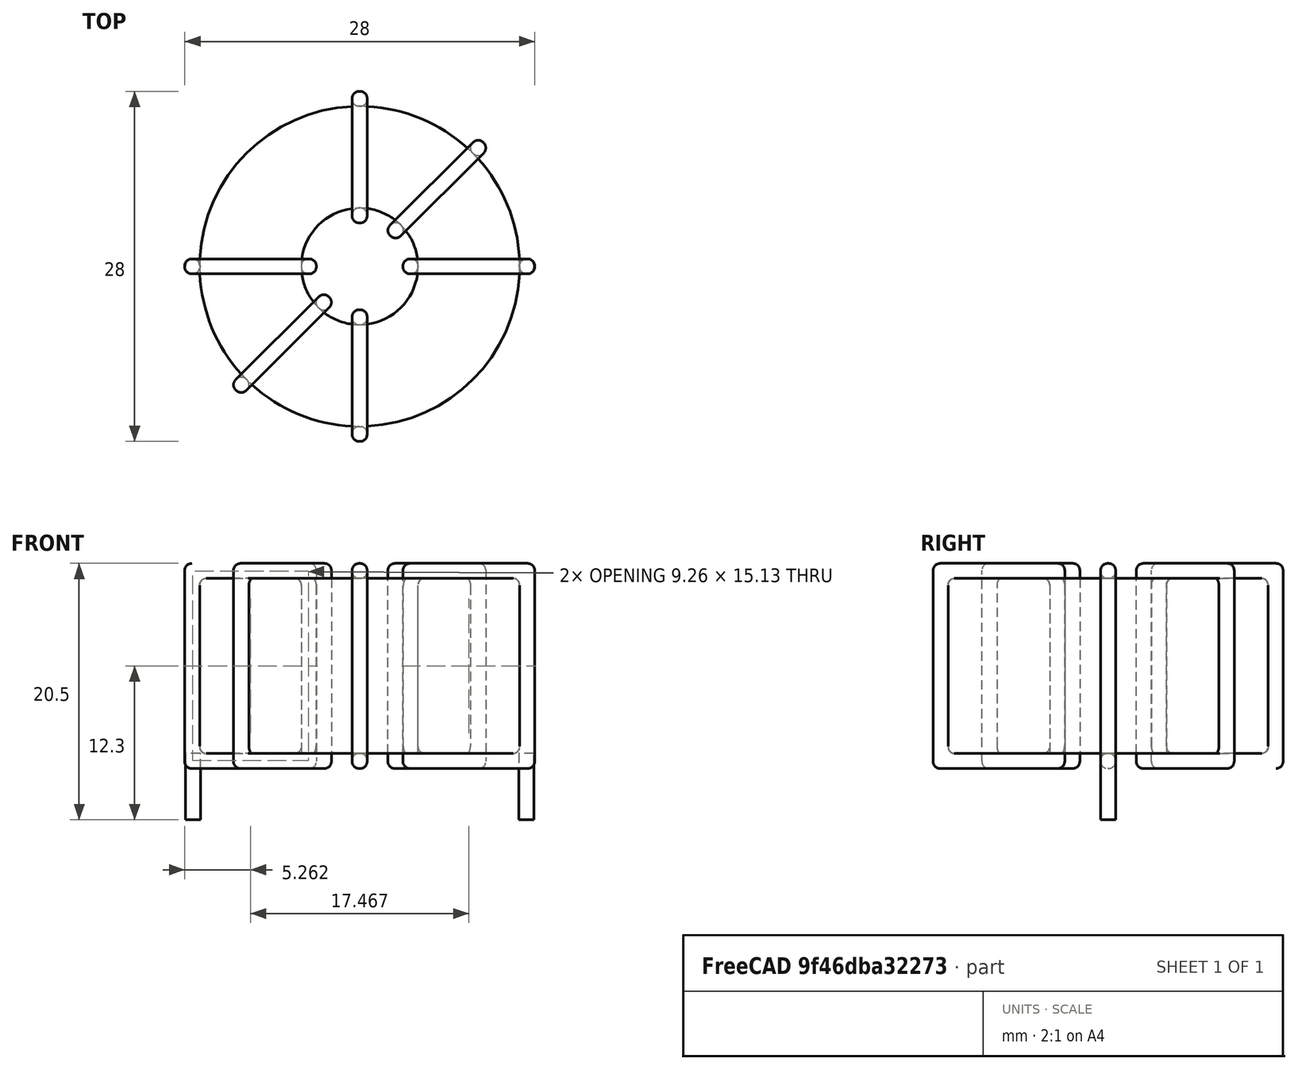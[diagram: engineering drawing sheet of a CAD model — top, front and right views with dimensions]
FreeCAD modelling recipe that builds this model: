
FCSTD DOCUMENT  (FreeCAD 0.16R6703 (Git))
Label: L_Toroid_Horizontal_D28.0mm_P26.67mm_Bourns_2200series
License: All rights reserved
LicenseURL: http://en.wikipedia.org/wiki/All_rights_reserved
objects: Sketcher::SketchObject×6, PartDesign::Pad×6, PartDesign::Fillet×5, Spreadsheet::Sheet×1
note: 23 computed .brp shape members not serialized (recipe doc carries the construction recipe); baked Part::Feature solids carry a one-line shape summary decoded from their .brp

FEATURE [Spreadsheet::Sheet] Spreadsheet  label="dimensions"
  cells = A1=Wx; B1(Wx)=28; C1(WW)=9.333333333333334; D1=28; A2=Wy; B2(Wy)=28; D2=28; A3=RM; B3(RMx)=26.67; C3(RMy)=0; A4=d_wire; B4(d_wire)=1.2; A5=H; B5(H)=14; A6=offsetx; B6(offsetx)=0.6649999999999992
FEATURE [Sketcher::SketchObject] Sketch
  Placement = pos=(0,0,1.7) rot=(0,0,1;0rad)
  expr: Placement.Base.z = 0.5 + Spreadsheet.d_wire
  expr: Constraints[0] = Spreadsheet.Wx / 2 - Spreadsheet.d_wire
  expr: Constraints[4] = Spreadsheet.WW / 2
  expr: Constraints[2] = Spreadsheet.RMy / 2
  expr: Constraints[1] = Spreadsheet.RMx / 2
  sketch-geometry (2):
    g0: Circle CenterX=13.335 CenterY=0 CenterZ=0 NormalX=0 NormalY=0 NormalZ=1 Radius=12.8
    g1: Circle CenterX=13.335 CenterY=0 CenterZ=0 NormalX=0 NormalY=0 NormalZ=1 Radius=4.66667
  constraints (5):
    c: Radius(g0) = 12.8
    c: DistanceX(g-1,g0) = 13.335
    c: DistanceY(g-1,g0) = 0
    c: Coincident(g1,g0)
    c: Radius(g1) = 4.66667
FEATURE [PartDesign::Pad] Pad
  Length = 14
  Length2 = 100
  Placement = pos=(0,0,1.7) rot=(0,0,1;0rad)
  Sketch = -> Sketch
  Type = 0
  expr: Length = Spreadsheet.H
FEATURE [Sketcher::SketchObject] Sketch001
  Placement = pos=(0,0,1.1) rot=(0,0,1;0rad)
  expr: Placement.Base.z = 0.5 + Spreadsheet.d_wire * 0.5
  expr: Constraints[4] = Spreadsheet.RMx
  expr: Constraints[2] = Spreadsheet.RMy
  expr: Constraints[1] = Spreadsheet.d_wire / 2
  sketch-geometry (2):
    g0: Circle CenterX=0 CenterY=0 CenterZ=0 NormalX=0 NormalY=0 NormalZ=1 Radius=0.6
    g1: Circle CenterX=26.67 CenterY=0 CenterZ=0 NormalX=0 NormalY=0 NormalZ=1 Radius=0.6
  constraints (5):
    c: Equal(g0,g1)
    c: Radius(g0) = 0.6
    c: DistanceY(g-1,g1) = 0
    c: Coincident(g0,g-1)
    c: DistanceX(g-1,g1) = 26.67
FEATURE [PartDesign::Pad] Pad001
  Length = 0.6
  Length2 = 4.7
  Placement = pos=(0,0,1.1) rot=(0,0,1;0rad)
  Reversed = true
  Sketch = -> Sketch001
  Type = 4
  expr: Length2 = 3.5 + Spreadsheet.d_wire
  expr: Length = Spreadsheet.d_wire / 2
FEATURE [PartDesign::Fillet] Fillet
  Base = -> Pad [Edge6,Edge3,Edge2]
  Placement = pos=(0,0,1.7) rot=(0,0,1;0rad)
  Radius = 0.5
FEATURE [Sketcher::SketchObject] Sketch003
  Placement = pos=(13.335,0,0) rot=(1,0,0;1.5708rad)
  expr: Placement.Base.x = Spreadsheet.RMx / 2
  expr: Constraints[49] = Spreadsheet.Wx - Spreadsheet.d_wire * 2
  expr: Constraints[44] = Spreadsheet.d_wire
  expr: Constraints[23] = Spreadsheet.H
  expr: Constraints[22] = Spreadsheet.Wx / 2 - Spreadsheet.d_wire
  expr: Placement.Base.y = Spreadsheet.RMy / 2
  expr: Constraints[21] = (Spreadsheet.Wx - Spreadsheet.WW) / 2 - Spreadsheet.d_wire
  expr: Constraints[19] = Spreadsheet.d_wire
  expr: Constraints[17] = Spreadsheet.d_wire
  expr: Constraints[18] = Spreadsheet.d_wire
  expr: Constraints[16] = Spreadsheet.d_wire
  sketch-geometry (16):
    g0: LineSegment StartX=-3.46667 StartY=0.5 StartZ=0 EndX=-14 EndY=0.5 EndZ=0
    g1: LineSegment StartX=-14 StartY=0.5 StartZ=0 EndX=-14 EndY=16.9 EndZ=0
    g2: LineSegment StartX=-14 StartY=16.9 StartZ=0 EndX=-3.46667 EndY=16.9 EndZ=0
    g3: LineSegment StartX=-3.46667 StartY=16.9 StartZ=0 EndX=-3.46667 EndY=0.5 EndZ=0
    g4: LineSegment StartX=-12.8 StartY=15.7 StartZ=0 EndX=-4.66667 EndY=15.7 EndZ=0
    g5: LineSegment StartX=-4.66667 StartY=15.7 StartZ=0 EndX=-4.66667 EndY=1.7 EndZ=0
    g6: LineSegment StartX=-4.66667 StartY=1.7 StartZ=0 EndX=-12.8 EndY=1.7 EndZ=0
    g7: LineSegment StartX=-12.8 StartY=1.7 StartZ=0 EndX=-12.8 EndY=15.7 EndZ=0
    g8: LineSegment StartX=3.46667 StartY=16.9 StartZ=0 EndX=14 EndY=16.9 EndZ=0
    g9: LineSegment StartX=14 StartY=16.9 StartZ=0 EndX=14 EndY=0.5 EndZ=0
    g10: LineSegment StartX=14 StartY=0.5 StartZ=0 EndX=3.46667 EndY=0.5 EndZ=0
    g11: LineSegment StartX=3.46667 StartY=0.5 StartZ=0 EndX=3.46667 EndY=16.9 EndZ=0
    g12: LineSegment StartX=4.66667 StartY=15.7 StartZ=0 EndX=12.8 EndY=15.7 EndZ=0
    g13: LineSegment StartX=12.8 StartY=15.7 StartZ=0 EndX=12.8 EndY=1.7 EndZ=0
    g14: LineSegment StartX=12.8 StartY=1.7 StartZ=0 EndX=4.66667 EndY=1.7 EndZ=0
    g15: LineSegment StartX=4.66667 StartY=1.7 StartZ=0 EndX=4.66667 EndY=15.7 EndZ=0
  constraints (50):
    c: Horizontal(g0)
    c: Coincident(g1,g0)
    c: Vertical(g1)
    c: Coincident(g2,g1)
    c: Horizontal(g2)
    c: Coincident(g3,g2)
    c: Coincident(g3,g0)
    c: Vertical(g3)
    c: Coincident(g4,g5)
    c: Coincident(g5,g6)
    c: Coincident(g6,g7)
    c: Coincident(g7,g4)
    c: Horizontal(g4)
    c: Horizontal(g6)
    c: Vertical(g5)
    c: Vertical(g7)
    c: DistanceX(g1,g4) = 1.2
    c: DistanceY(g4,g1) = 1.2
    c: DistanceX(g5,g0) = 1.2
    c: DistanceY(g0,g5) = 1.2
    c: DistanceY(g-1,g0) = 0.5
    c: DistanceX(g6,g6) = 8.13333
    c: DistanceX(g6,g-1) = 12.8
    c: DistanceY(g7,g7) = 14
    c: Coincident(g8,g9)
    c: Coincident(g9,g10)
    c: Coincident(g10,g11)
    c: Coincident(g11,g8)
    c: Horizontal(g8)
    c: Horizontal(g10)
    c: Vertical(g9)
    c: Vertical(g11)
    c: Coincident(g12,g13)
    c: Coincident(g13,g14)
    c: Coincident(g14,g15)
    c: Coincident(g15,g12)
    c: Horizontal(g12)
    c: Horizontal(g14)
    c: Vertical(g13)
    c: Vertical(g15)
    c: DistanceY(g8,g2) = 0
    c: DistanceY(g10,g0) = 0
    c: DistanceY(g14,g5) = 0
    c: DistanceY(g12,g4) = 0
    c: DistanceX(g8,g12) = 1.2
    c: Equal(g8,g2)
    c: Equal(g12,g4)
    c: Equal(g9,g1)
    c: Equal(g13,g7)
    c: DistanceX(g4,g12) = 25.6
FEATURE [PartDesign::Pad] Pad002
  Length = 1.2
  Length2 = 100
  Midplane = true
  Placement = pos=(13.335,0,0) rot=(1,0,0;1.5708rad)
  Sketch = -> Sketch003
  Type = 0
  expr: Length = Spreadsheet.d_wire
FEATURE [PartDesign::Fillet] Fillet001
  Base = -> Pad002 [Edge38,Edge41,Edge42,Edge43,Edge29,Edge32,Edge33,Edge34,Edge25,Edge35,Edge36,Edge13,Edge14,Edge15,Edge16,Edge17,Edge18,Edge19,Edge1,Edge2,Edge3,Edge4,Edge5,Edge6,Edge7,Edge37,Edge39,Edge40,Edge20,Edge23,Edge24,Edge21,Edge22,Edge8,Edge9,Edge10,Edge11,Edge12,Edge26,Edge27,+8 more]
  Placement = pos=(13.335,0,0) rot=(1,0,0;1.5708rad)
  Radius = 0.564
  expr: Radius = Spreadsheet.d_wire * 0.47
FEATURE [Sketcher::SketchObject] Sketch004
  Placement = pos=(13.335,0,0) rot=(0.862856,0.357407,0.357407;1.71777rad)
  expr: Placement.Base.x = Spreadsheet.RMx / 2
  expr: Constraints[49] = Spreadsheet.Wx - 2 * Spreadsheet.d_wire
  expr: Constraints[44] = Spreadsheet.d_wire
  expr: Constraints[23] = Spreadsheet.H
  expr: Constraints[22] = Spreadsheet.Wx / 2 - Spreadsheet.d_wire
  expr: Placement.Base.y = Spreadsheet.RMy / 2
  expr: Constraints[21] = (Spreadsheet.Wx - Spreadsheet.WW) / 2 - Spreadsheet.d_wire
  expr: Constraints[19] = Spreadsheet.d_wire
  expr: Constraints[17] = Spreadsheet.d_wire
  expr: Constraints[18] = Spreadsheet.d_wire
  expr: Constraints[16] = Spreadsheet.d_wire
  sketch-geometry (16):
    g0: LineSegment StartX=-3.46667 StartY=0.5 StartZ=0 EndX=-14 EndY=0.5 EndZ=0
    g1: LineSegment StartX=-14 StartY=0.5 StartZ=0 EndX=-14 EndY=16.9 EndZ=0
    g2: LineSegment StartX=-14 StartY=16.9 StartZ=0 EndX=-3.46667 EndY=16.9 EndZ=0
    g3: LineSegment StartX=-3.46667 StartY=16.9 StartZ=0 EndX=-3.46667 EndY=0.5 EndZ=0
    g4: LineSegment StartX=-12.8 StartY=15.7 StartZ=0 EndX=-4.66667 EndY=15.7 EndZ=0
    g5: LineSegment StartX=-4.66667 StartY=15.7 StartZ=0 EndX=-4.66667 EndY=1.7 EndZ=0
    g6: LineSegment StartX=-4.66667 StartY=1.7 StartZ=0 EndX=-12.8 EndY=1.7 EndZ=0
    g7: LineSegment StartX=-12.8 StartY=1.7 StartZ=0 EndX=-12.8 EndY=15.7 EndZ=0
    g8: LineSegment StartX=3.46667 StartY=16.9 StartZ=0 EndX=14 EndY=16.9 EndZ=0
    g9: LineSegment StartX=14 StartY=16.9 StartZ=0 EndX=14 EndY=0.5 EndZ=0
    g10: LineSegment StartX=14 StartY=0.5 StartZ=0 EndX=3.46667 EndY=0.5 EndZ=0
    g11: LineSegment StartX=3.46667 StartY=0.5 StartZ=0 EndX=3.46667 EndY=16.9 EndZ=0
    g12: LineSegment StartX=4.66667 StartY=15.7 StartZ=0 EndX=12.8 EndY=15.7 EndZ=0
    g13: LineSegment StartX=12.8 StartY=15.7 StartZ=0 EndX=12.8 EndY=1.7 EndZ=0
    g14: LineSegment StartX=12.8 StartY=1.7 StartZ=0 EndX=4.66667 EndY=1.7 EndZ=0
    g15: LineSegment StartX=4.66667 StartY=1.7 StartZ=0 EndX=4.66667 EndY=15.7 EndZ=0
  constraints (50):
    c: Horizontal(g0)
    c: Coincident(g1,g0)
    c: Vertical(g1)
    c: Coincident(g2,g1)
    c: Horizontal(g2)
    c: Coincident(g3,g2)
    c: Coincident(g3,g0)
    c: Vertical(g3)
    c: Coincident(g4,g5)
    c: Coincident(g5,g6)
    c: Coincident(g6,g7)
    c: Coincident(g7,g4)
    c: Horizontal(g4)
    c: Horizontal(g6)
    c: Vertical(g5)
    c: Vertical(g7)
    c: DistanceX(g1,g4) = 1.2
    c: DistanceY(g4,g1) = 1.2
    c: DistanceX(g5,g0) = 1.2
    c: DistanceY(g0,g5) = 1.2
    c: DistanceY(g-1,g0) = 0.5
    c: DistanceX(g6,g6) = 8.13333
    c: DistanceX(g6,g-1) = 12.8
    c: DistanceY(g7,g7) = 14
    c: Coincident(g8,g9)
    c: Coincident(g9,g10)
    c: Coincident(g10,g11)
    c: Coincident(g11,g8)
    c: Horizontal(g8)
    c: Horizontal(g10)
    c: Vertical(g9)
    c: Vertical(g11)
    c: Coincident(g12,g13)
    c: Coincident(g13,g14)
    c: Coincident(g14,g15)
    c: Coincident(g15,g12)
    c: Horizontal(g12)
    c: Horizontal(g14)
    c: Vertical(g13)
    c: Vertical(g15)
    c: DistanceY(g8,g2) = 0
    c: DistanceY(g10,g0) = 0
    c: DistanceY(g14,g5) = 0
    c: DistanceY(g12,g4) = 0
    c: DistanceX(g8,g12) = 1.2
    c: Equal(g8,g2)
    c: Equal(g12,g4)
    c: Equal(g9,g1)
    c: Equal(g13,g7)
    c: DistanceX(g4,g12) = 25.6
FEATURE [PartDesign::Pad] Pad003
  Length = 1.2
  Length2 = 100
  Midplane = true
  Placement = pos=(13.335,0,0) rot=(0.862856,0.357407,0.357407;1.71777rad)
  Sketch = -> Sketch004
  Type = 0
  expr: Length = Spreadsheet.d_wire
FEATURE [PartDesign::Fillet] Fillet002
  Base = -> Pad003 [Edge38,Edge41,Edge42,Edge43,Edge29,Edge32,Edge33,Edge34,Edge25,Edge35,Edge36,Edge13,Edge14,Edge15,Edge16,Edge17,Edge18,Edge19,Edge1,Edge2,Edge3,Edge4,Edge5,Edge6,Edge7,Edge37,Edge39,Edge40,Edge20,Edge23,Edge24,Edge21,Edge22,Edge8,Edge9,Edge10,Edge11,Edge12,Edge26,Edge27,+8 more]
  Placement = pos=(13.335,0,0) rot=(0.862856,0.357407,0.357407;1.71777rad)
  Radius = 0.564
  expr: Radius = Spreadsheet.d_wire * 0.47
FEATURE [Sketcher::SketchObject] Sketch005
  Placement = pos=(13.335,0,0) rot=(0.862856,-0.357407,-0.357407;1.71777rad)
  expr: Placement.Base.x = Spreadsheet.RMx / 2
  expr: Constraints[49] = Spreadsheet.Wx - 2 * Spreadsheet.d_wire
  expr: Constraints[44] = Spreadsheet.d_wire
  expr: Constraints[23] = Spreadsheet.H
  expr: Constraints[22] = Spreadsheet.Wx / 2 - Spreadsheet.d_wire
  expr: Placement.Base.y = Spreadsheet.RMy / 2
  expr: Constraints[21] = (Spreadsheet.Wx - Spreadsheet.WW) / 2 - Spreadsheet.d_wire
  expr: Constraints[19] = Spreadsheet.d_wire
  expr: Constraints[17] = Spreadsheet.d_wire
  expr: Constraints[18] = Spreadsheet.d_wire
  expr: Constraints[16] = Spreadsheet.d_wire
  sketch-geometry (16):
    g0: LineSegment StartX=-3.46667 StartY=0.5 StartZ=0 EndX=-14 EndY=0.5 EndZ=0
    g1: LineSegment StartX=-14 StartY=0.5 StartZ=0 EndX=-14 EndY=16.9 EndZ=0
    g2: LineSegment StartX=-14 StartY=16.9 StartZ=0 EndX=-3.46667 EndY=16.9 EndZ=0
    g3: LineSegment StartX=-3.46667 StartY=16.9 StartZ=0 EndX=-3.46667 EndY=0.5 EndZ=0
    g4: LineSegment StartX=-12.8 StartY=15.7 StartZ=0 EndX=-4.66667 EndY=15.7 EndZ=0
    g5: LineSegment StartX=-4.66667 StartY=15.7 StartZ=0 EndX=-4.66667 EndY=1.7 EndZ=0
    g6: LineSegment StartX=-4.66667 StartY=1.7 StartZ=0 EndX=-12.8 EndY=1.7 EndZ=0
    g7: LineSegment StartX=-12.8 StartY=1.7 StartZ=0 EndX=-12.8 EndY=15.7 EndZ=0
    g8: LineSegment StartX=3.46667 StartY=16.9 StartZ=0 EndX=14 EndY=16.9 EndZ=0
    g9: LineSegment StartX=14 StartY=16.9 StartZ=0 EndX=14 EndY=0.5 EndZ=0
    g10: LineSegment StartX=14 StartY=0.5 StartZ=0 EndX=3.46667 EndY=0.5 EndZ=0
    g11: LineSegment StartX=3.46667 StartY=0.5 StartZ=0 EndX=3.46667 EndY=16.9 EndZ=0
    g12: LineSegment StartX=4.66667 StartY=15.7 StartZ=0 EndX=12.8 EndY=15.7 EndZ=0
    g13: LineSegment StartX=12.8 StartY=15.7 StartZ=0 EndX=12.8 EndY=1.7 EndZ=0
    g14: LineSegment StartX=12.8 StartY=1.7 StartZ=0 EndX=4.66667 EndY=1.7 EndZ=0
    g15: LineSegment StartX=4.66667 StartY=1.7 StartZ=0 EndX=4.66667 EndY=15.7 EndZ=0
  constraints (50):
    c: Horizontal(g0)
    c: Coincident(g1,g0)
    c: Vertical(g1)
    c: Coincident(g2,g1)
    c: Horizontal(g2)
    c: Coincident(g3,g2)
    c: Coincident(g3,g0)
    c: Vertical(g3)
    c: Coincident(g4,g5)
    c: Coincident(g5,g6)
    c: Coincident(g6,g7)
    c: Coincident(g7,g4)
    c: Horizontal(g4)
    c: Horizontal(g6)
    c: Vertical(g5)
    c: Vertical(g7)
    c: DistanceX(g1,g4) = 1.2
    c: DistanceY(g4,g1) = 1.2
    c: DistanceX(g5,g0) = 1.2
    c: DistanceY(g0,g5) = 1.2
    c: DistanceY(g-1,g0) = 0.5
    c: DistanceX(g6,g6) = 8.13333
    c: DistanceX(g6,g-1) = 12.8
    c: DistanceY(g7,g7) = 14
    c: Coincident(g8,g9)
    c: Coincident(g9,g10)
    c: Coincident(g10,g11)
    c: Coincident(g11,g8)
    c: Horizontal(g8)
    c: Horizontal(g10)
    c: Vertical(g9)
    c: Vertical(g11)
    c: Coincident(g12,g13)
    c: Coincident(g13,g14)
    c: Coincident(g14,g15)
    c: Coincident(g15,g12)
    c: Horizontal(g12)
    c: Horizontal(g14)
    c: Vertical(g13)
    c: Vertical(g15)
    c: DistanceY(g8,g2) = 0
    c: DistanceY(g10,g0) = 0
    c: DistanceY(g14,g5) = 0
    c: DistanceY(g12,g4) = 0
    c: DistanceX(g8,g12) = 1.2
    c: Equal(g8,g2)
    c: Equal(g12,g4)
    c: Equal(g9,g1)
    c: Equal(g13,g7)
    c: DistanceX(g4,g12) = 25.6
FEATURE [PartDesign::Pad] Pad004
  Length = 1.2
  Length2 = 100
  Midplane = true
  Placement = pos=(13.335,0,0) rot=(0.862856,-0.357407,-0.357407;1.71777rad)
  Sketch = -> Sketch005
  Type = 0
  expr: Length = Spreadsheet.d_wire
FEATURE [PartDesign::Fillet] Fillet003
  Base = -> Pad004 [Edge38,Edge41,Edge42,Edge43,Edge29,Edge32,Edge33,Edge34,Edge25,Edge35,Edge36,Edge13,Edge14,Edge15,Edge16,Edge17,Edge18,Edge19,Edge1,Edge2,Edge3,Edge4,Edge5,Edge6,Edge7,Edge37,Edge39,Edge40,Edge20,Edge23,Edge24,Edge21,Edge22,Edge8,Edge9,Edge10,Edge11,Edge12,Edge26,Edge27,+8 more]
  Placement = pos=(13.335,0,0) rot=(0.862856,-0.357407,-0.357407;1.71777rad)
  Radius = 0.564
  expr: Radius = Spreadsheet.d_wire * 0.47
FEATURE [Sketcher::SketchObject] Sketch006
  Placement = pos=(13.335,0,0) rot=(0.57735,0.57735,0.57735;2.0944rad)
  expr: Placement.Base.x = Spreadsheet.RMx / 2
  expr: Constraints[49] = Spreadsheet.Wx - Spreadsheet.d_wire * 2
  expr: Constraints[44] = Spreadsheet.d_wire
  expr: Constraints[23] = Spreadsheet.H
  expr: Constraints[22] = Spreadsheet.Wx / 2 - Spreadsheet.d_wire
  expr: Placement.Base.y = Spreadsheet.RMy / 2
  expr: Constraints[21] = (Spreadsheet.Wx - Spreadsheet.WW) / 2 - Spreadsheet.d_wire
  expr: Constraints[19] = Spreadsheet.d_wire
  expr: Constraints[17] = Spreadsheet.d_wire
  expr: Constraints[18] = Spreadsheet.d_wire
  expr: Constraints[16] = Spreadsheet.d_wire
  sketch-geometry (16):
    g0: LineSegment StartX=-3.46667 StartY=0.5 StartZ=0 EndX=-14 EndY=0.5 EndZ=0
    g1: LineSegment StartX=-14 StartY=0.5 StartZ=0 EndX=-14 EndY=16.9 EndZ=0
    g2: LineSegment StartX=-14 StartY=16.9 StartZ=0 EndX=-3.46667 EndY=16.9 EndZ=0
    g3: LineSegment StartX=-3.46667 StartY=16.9 StartZ=0 EndX=-3.46667 EndY=0.5 EndZ=0
    g4: LineSegment StartX=-12.8 StartY=15.7 StartZ=0 EndX=-4.66667 EndY=15.7 EndZ=0
    g5: LineSegment StartX=-4.66667 StartY=15.7 StartZ=0 EndX=-4.66667 EndY=1.7 EndZ=0
    g6: LineSegment StartX=-4.66667 StartY=1.7 StartZ=0 EndX=-12.8 EndY=1.7 EndZ=0
    g7: LineSegment StartX=-12.8 StartY=1.7 StartZ=0 EndX=-12.8 EndY=15.7 EndZ=0
    g8: LineSegment StartX=3.46667 StartY=16.9 StartZ=0 EndX=14 EndY=16.9 EndZ=0
    g9: LineSegment StartX=14 StartY=16.9 StartZ=0 EndX=14 EndY=0.5 EndZ=0
    g10: LineSegment StartX=14 StartY=0.5 StartZ=0 EndX=3.46667 EndY=0.5 EndZ=0
    g11: LineSegment StartX=3.46667 StartY=0.5 StartZ=0 EndX=3.46667 EndY=16.9 EndZ=0
    g12: LineSegment StartX=4.66667 StartY=15.7 StartZ=0 EndX=12.8 EndY=15.7 EndZ=0
    g13: LineSegment StartX=12.8 StartY=15.7 StartZ=0 EndX=12.8 EndY=1.7 EndZ=0
    g14: LineSegment StartX=12.8 StartY=1.7 StartZ=0 EndX=4.66667 EndY=1.7 EndZ=0
    g15: LineSegment StartX=4.66667 StartY=1.7 StartZ=0 EndX=4.66667 EndY=15.7 EndZ=0
  constraints (50):
    c: Horizontal(g0)
    c: Coincident(g1,g0)
    c: Vertical(g1)
    c: Coincident(g2,g1)
    c: Horizontal(g2)
    c: Coincident(g3,g2)
    c: Coincident(g3,g0)
    c: Vertical(g3)
    c: Coincident(g4,g5)
    c: Coincident(g5,g6)
    c: Coincident(g6,g7)
    c: Coincident(g7,g4)
    c: Horizontal(g4)
    c: Horizontal(g6)
    c: Vertical(g5)
    c: Vertical(g7)
    c: DistanceX(g1,g4) = 1.2
    c: DistanceY(g4,g1) = 1.2
    c: DistanceX(g5,g0) = 1.2
    c: DistanceY(g0,g5) = 1.2
    c: DistanceY(g-1,g0) = 0.5
    c: DistanceX(g6,g6) = 8.13333
    c: DistanceX(g6,g-1) = 12.8
    c: DistanceY(g7,g7) = 14
    c: Coincident(g8,g9)
    c: Coincident(g9,g10)
    c: Coincident(g10,g11)
    c: Coincident(g11,g8)
    c: Horizontal(g8)
    c: Horizontal(g10)
    c: Vertical(g9)
    c: Vertical(g11)
    c: Coincident(g12,g13)
    c: Coincident(g13,g14)
    c: Coincident(g14,g15)
    c: Coincident(g15,g12)
    c: Horizontal(g12)
    c: Horizontal(g14)
    c: Vertical(g13)
    c: Vertical(g15)
    c: DistanceY(g8,g2) = 0
    c: DistanceY(g10,g0) = 0
    c: DistanceY(g14,g5) = 0
    c: DistanceY(g12,g4) = 0
    c: DistanceX(g8,g12) = 1.2
    c: Equal(g8,g2)
    c: Equal(g12,g4)
    c: Equal(g9,g1)
    c: Equal(g13,g7)
    c: DistanceX(g4,g12) = 25.6
FEATURE [PartDesign::Pad] Pad005
  Length = 1.2
  Length2 = 100
  Midplane = true
  Placement = pos=(13.335,0,0) rot=(0.57735,0.57735,0.57735;2.0944rad)
  Sketch = -> Sketch006
  Type = 0
  expr: Length = Spreadsheet.d_wire
FEATURE [PartDesign::Fillet] Fillet004
  Base = -> Pad005 [Edge38,Edge41,Edge42,Edge43,Edge29,Edge32,Edge33,Edge34,Edge25,Edge35,Edge36,Edge13,Edge14,Edge15,Edge16,Edge17,Edge18,Edge19,Edge1,Edge2,Edge3,Edge4,Edge5,Edge6,Edge7,Edge37,Edge39,Edge40,Edge20,Edge23,Edge24,Edge21,Edge22,Edge8,Edge9,Edge10,Edge11,Edge12,Edge26,Edge27,+8 more]
  Placement = pos=(13.335,0,0) rot=(0.57735,0.57735,0.57735;2.0944rad)
  Radius = 0.564
  expr: Radius = Spreadsheet.d_wire * 0.47
